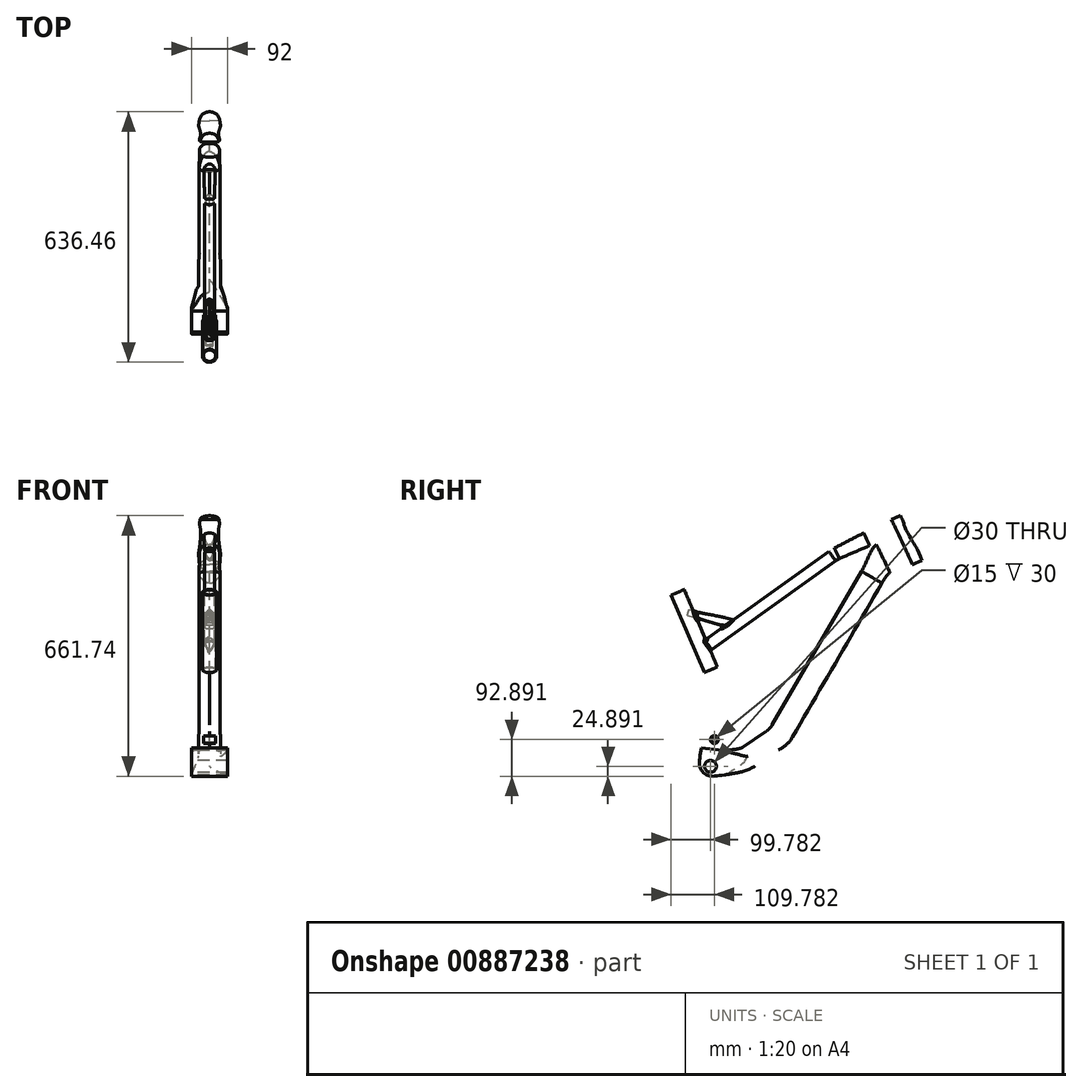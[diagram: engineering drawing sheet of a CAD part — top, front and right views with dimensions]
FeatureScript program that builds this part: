
annotation { "Feature Type Name" : "Feature", "Feature Type Description" : "" }
export const myFeature = defineFeature(function(context is Context, id is Id, definition is map)
    precondition{}
    {
        {
            var Q0;
            Q0=qCreatedBy(makeId("Right.planeOp"),FACE);
            var sketch = newSketch(context, id + "F0", { "sketchPlane" : qUnion([Q0])});
            skLineSegment(sketch, "E0", {"start": v(394.56, 392.73) * mm, "end": v(268.92, 334.44) * mm});
            skLineSegment(sketch, "E1", {"start": v(268.92, 334.44) * mm, "end": v(-58.18, 97.5) * mm});
            skLineSegment(sketch, "E2", {"start": v(359.7, 337.97) * mm, "end": v(273.68, 299.57) * mm});
            skLineSegment(sketch, "E3", {"start": v(273.68, 299.57) * mm, "end": v(-46.2, 69.7) * mm});
            skLineSegment(sketch, "E4", {"start": v(-106.05, 214.72) * mm, "end": v(-58.18, 103.33) * mm});
            skLineSegment(sketch, "E5", {"start": v(-138.56, 202.1) * mm, "end": v(-48.82, -12.93) * mm});
            skLineSegment(sketch, "E6", {"start": v(24.33, -178.16) * mm, "end": v(95.53, -133.4) * mm});
            skLineSegment(sketch, "E7", {"start": v(95.53, -133.4) * mm, "end": v(106.59, -124.69) * mm});
            skLineSegment(sketch, "E8", {"start": v(106.59, -124.69) * mm, "end": v(115.3, -114.9) * mm});
            skLineSegment(sketch, "E9", {"start": v(115.3, -114.9) * mm, "end": v(371.01, 330.47) * mm});
            skLineSegment(sketch, "E10", {"start": v(492.3, 300.77) * mm, "end": v(414.97, 263.1) * mm});
            skLineSegment(sketch, "E11", {"start": v(414.97, 263.1) * mm, "end": v(406.05, 257.63) * mm});
            skLineSegment(sketch, "E12", {"start": v(406.05, 257.63) * mm, "end": v(398.23, 251.01) * mm});
            skLineSegment(sketch, "E13", {"start": v(398.23, 251.01) * mm, "end": v(391.73, 242.37) * mm});
            skLineSegment(sketch, "E14", {"start": v(391.73, 242.37) * mm, "end": v(164.62, -148.47) * mm});
            skLineSegment(sketch, "E15", {"start": v(164.62, -148.47) * mm, "end": v(157.35, -161.15) * mm});
            skLineSegment(sketch, "E16", {"start": v(157.35, -161.15) * mm, "end": v(146.9, -170) * mm});
            skLineSegment(sketch, "E17", {"start": v(146.9, -170) * mm, "end": v(129.26, -182.49) * mm});
            skLineSegment(sketch, "E18", {"start": v(129.26, -182.49) * mm, "end": v(69.06, -222.74) * mm});
            skLineSegment(sketch, "E19", {"start": v(-65.83, -137.88) * mm, "end": v(-59.08, -90.58) * mm});
            skLineSegment(sketch, "E20", {"start": v(-59.08, -90.58) * mm, "end": v(-49.16, -39.89) * mm});
            skLineSegment(sketch, "E21", {"start": v(-49.16, -39.89) * mm, "end": v(-47.14, -26.82) * mm});
            skLineSegment(sketch, "E22", {"start": v(2.2, 4.26) * mm, "end": v(-21.46, -107.7) * mm});
            skLineSegment(sketch, "E23", {"start": v(-78.37, 170.94) * mm, "end": v(2.72, 153.82) * mm});
            skLineSegment(sketch, "E24", {"start": v(-78.8, 154.84) * mm, "end": v(-10.87, 135.06) * mm});
            skLineSegment(sketch, "E25", {"start": v(437.67, 414) * mm, "end": v(393.8, 394.32) * mm});
            skLineSegment(sketch, "E26", {"start": v(415.73, 404.16) * mm, "end": v(-44.38, 404.16) * mm});
            skLineSegment(sketch, "E27", {"start": v(-44.38, -222.84) * mm, "end": v(-44.38, 470.33) * mm});
            skLineSegment(sketch, "E28", {"start": v(-44.38, -222.84) * mm, "end": v(-220.5, 433.45) * mm});
            skLineSegment(sketch, "E29", {"start": v(-44.38, -222.84) * mm, "end": v(-34.38, -154.84) * mm});
            skCircle(sketch, "E30", {"center": v(-34.38, -154.84) * mm, "radius": 10 * mm});
            skCircle(sketch, "E31", {"center": v(-34.38, -154.84) * mm, "radius": 7.5 * mm});
            skLineSegment(sketch, "E32", {"start": v(415.73, 404.16) * mm, "end": v(497.16, 229.55) * mm});
            skPoint(sketch, "E33", {"position": v(422.14, 390.42) * mm});
            skPoint(sketch, "E34", {"position": v(432.88, 367.4) * mm});
            skPoint(sketch, "E35", {"position": v(454.56, 320.9) * mm});
            skPoint(sketch, "E36", {"position": v(469.2, 289.52) * mm});
            skFitSpline(sketch, "E37", {"points": [v(437.67, 414) * mm, v(443.95, 402.74) * mm, v(445.2, 399.5) * mm, v(452.3, 378.64) * mm, v(478.75, 333.33) * mm, v(480.29, 331) * mm, v(492.3, 300.77) * mm], "startDerivative": vector(88.16, -136) * mm, "endDerivative": vector(86.61, -241.27) * mm});
            skCircle(sketch, "E38", {"center": v(-44.38, -222.84) * mm, "radius": 15 * mm});
            skLineSegment(sketch, "E39", {"start": v(-13.68, -182.87) * mm, "end": v(-7.77, -244.28) * mm});
            skFitSpline(sketch, "E40", {"points": [v(-67.41, -175.9) * mm, v(-70.5, -226.93) * mm, v(-50.42, -245.86) * mm, v(-7.77, -244.28) * mm], "startDerivative": vector(-21.1, -148.4) * mm, "endDerivative": vector(183.55, 26.83) * mm});
            skLineSegment(sketch, "E41", {"start": v(-13.68, -182.87) * mm, "end": v(-67.41, -175.9) * mm});
            skFitSpline(sketch, "E42", {"points": [v(69.06, -222.74) * mm, v(33.55, -237.56) * mm, v(-7.77, -244.28) * mm], "startDerivative": vector(-87.67, -58.62) * mm, "endDerivative": vector(-97.3, -14.22) * mm});
            skSolve(sketch);
        }
        {
            var Q0;
            Q0=sQuery(id+"F0.wireOp",EDGE,"E14");
            var Q1;
            Q1=sQuery(id+"F0.wireOp",VERTEX,"E14.end");
            cPlane(context, id + "F1", {"entities" : qUnion([Q0, Q1]), "cplaneType" : CPlaneType.LINE_POINT, "offset" : 25 * mm, "width" : 150 * mm, "height" : 150 * mm});
        }
        {
            var Q0;
            Q0=qCreatedBy(id+"F1.planeOp",FACE);
            var sketch = newSketch(context, id + "F2", { "sketchPlane" : qUnion([Q0])});
            skFitSpline(sketch, "E43", {"points": [v(0, -216.2) * mm, v(11, -210.2) * mm, v(26, -168.2) * mm, v(20, -160.7) * mm, v(0, -156.2) * mm], "startDerivative": vector(27.72, -0.05) * mm, "endDerivative": vector(-102.66, 1.52) * mm});
            skLineSegment(sketch, "E44", {"start": v(0, 0) * mm, "end": v(0, -298.68) * mm});
            skFitSpline(sketch, "E45.MirrorCS", {"points": [v(0, -216.2) * mm, v(-11, -210.2) * mm, v(-26, -168.2) * mm, v(-20, -160.7) * mm, v(0, -156.2) * mm], "startDerivative": vector(-27.72, -0.05) * mm, "endDerivative": vector(102.66, 1.52) * mm});
            skSolve(sketch);
        }
        {
            var Q0;
            {var subQ0=sQuery(id+"F2.wireOp",EDGE,"E43");Q0=makeQuery(id+"F2.imprint","IMPRINT",FACE,{"disambiguationData":[TD([[makeQuery(id+"F2.imprint","IMPRINT",EDGE,{"derivedFrom":subQ0}),1.0]])]});}
            var Q1;
            {var subQ0=sQuery(id+"F2.wireOp",EDGE,"E45.MirrorCS");Q1=makeQuery(id+"F2.imprint","IMPRINT",FACE,{"disambiguationData":[TD([[makeQuery(id+"F2.imprint","IMPRINT",EDGE,{"derivedFrom":subQ0}),-1.0]])]});}
            var Q2;
            Q2=sQuery(id+"F0.wireOp",EDGE,"E14");
            sweep(context, id + "F3", {"profiles" : qUnion([Q0, Q1]), "path" : qUnion([Q2])});
        }
        {
            var Q0;
            Q0=sQuery(id+"F0.wireOp",VERTEX,"E18.end");
            var Q1;
            Q1=sQuery(id+"F0.wireOp",EDGE,"E18");
            cPlane(context, id + "F4", {"entities" : qUnion([Q0, Q1]), "cplaneType" : CPlaneType.LINE_POINT, "offset" : 25 * mm, "width" : 150 * mm, "height" : 150 * mm});
        }
        {
            var Q0;
            Q0=qCreatedBy(id+"F4.planeOp",FACE);
            var sketch = newSketch(context, id + "F5", { "sketchPlane" : qUnion([Q0])});
            skFitSpline(sketch, "E46", {"points": [v(0, -222.4) * mm, v(15.02, -221) * mm, v(24.08, -211.48) * mm, v(26.32, -171.97) * mm, v(21.9, -167.33) * mm, v(0, -165.4) * mm], "startDerivative": vector(103.75, 0.01) * mm, "endDerivative": vector(-157.98, 1.47) * mm});
            skFitSpline(sketch, "E47.MirrorCS", {"points": [v(0, -222.4) * mm, v(-15.02, -221) * mm, v(-24.08, -211.48) * mm, v(-26.32, -171.97) * mm, v(-21.9, -167.33) * mm, v(0, -165.4) * mm], "startDerivative": vector(-103.75, 0.01) * mm, "endDerivative": vector(157.98, 1.47) * mm});
            skSolve(sketch);
        }
        {
            var Q0;
            Q0=makeQuery(id+"F5.imprint","IMPRINT",FACE,{"disambiguationData":[TD([[makeQuery(id+"F5.imprint","IMPRINT",EDGE,{"derivedFrom":sQuery(id+"F5.wireOp",EDGE,"E46")}),1.0]])]});
            var Q1;
            Q1=sQuery(id+"F0.wireOp",EDGE,"E18");
            sweep(context, id + "F6", {"profiles" : qUnion([Q0]), "path" : qUnion([Q1])});
        }
        {
            var Q0;
            Q0=makeQuery(id+"F6.opSweep","CAP_FACE",FACE,{"disambiguationData":[OSD([sQuery(id+"F0.wireOp",VERTEX,"E18.start"),sQuery(id+"F5.wireOp",EDGE,"E46"),sQuery(id+"F5.wireOp",EDGE,"E47.MirrorCS")])],"isStart":false});
            var Q1;
            Q1=makeQuery(id+"F3.opSweep","CAP_FACE",FACE,{"disambiguationData":[OSD([sQuery(id+"F0.wireOp",VERTEX,"E14.end"),sQuery(id+"F2.wireOp",EDGE,"E43"),sQuery(id+"F2.wireOp",EDGE,"E45.MirrorCS")])],"isStart":true});
            loft(context, id + "F7", {"operationType" : NewBodyOperationType.ADD, "startCondition" : LoftEndDerivativeType.MATCH_CURVATURE, "startMagnitude" : 1, "endCondition" : LoftEndDerivativeType.MATCH_CURVATURE, "endMagnitude" : 1, "sheetProfilesArray" : [{ "sheetProfileEntities" : qUnion([Q0]) }, { "sheetProfileEntities" : qUnion([Q1]) }]});
        }
        {
            var Q0;
            Q0=sQuery(id+"F0.wireOp",VERTEX,"E10.end");
            var Q1;
            Q1=sQuery(id+"F0.wireOp",EDGE,"E10");
            cPlane(context, id + "F8", {"entities" : qUnion([Q0, Q1]), "cplaneType" : CPlaneType.LINE_POINT, "offset" : 25 * mm, "width" : 150 * mm, "height" : 150 * mm});
        }
        {
            var Q0;
            Q0=qCreatedBy(id+"F8.planeOp",FACE);
            var sketch = newSketch(context, id + "F9", { "sketchPlane" : qUnion([Q0])});
            skFitSpline(sketch, "E48", {"points": [v(0, 62.13) * mm, v(-9.68, 63.52) * mm, v(-19.4, 73.38) * mm, v(-25.78, 107.3) * mm, v(-23.62, 126.27) * mm, v(-16.86, 137.13) * mm, v(0, 141.08) * mm], "startDerivative": vector(-109.37, 0) * mm, "endDerivative": vector(154.62, 0) * mm});
            skFitSpline(sketch, "E49.MirrorCS", {"points": [v(0, 62.13) * mm, v(9.68, 63.52) * mm, v(19.4, 73.38) * mm, v(25.78, 107.3) * mm, v(23.62, 126.27) * mm, v(16.86, 137.13) * mm, v(0, 141.08) * mm], "startDerivative": vector(109.37, 0) * mm, "endDerivative": vector(-154.62, 0) * mm});
            skSolve(sketch);
        }
        {
            var Q0;
            Q0=makeQuery(id+"F3.opSweep","CAP_FACE",FACE,{"disambiguationData":[OSD([sQuery(id+"F0.wireOp",VERTEX,"E14.start"),sQuery(id+"F2.wireOp",EDGE,"E43"),sQuery(id+"F2.wireOp",EDGE,"E45.MirrorCS")])],"isStart":false});
            var Q1;
            Q1=makeQuery(id+"F9.imprint","IMPRINT",FACE,{"disambiguationData":[TD([[makeQuery(id+"F9.imprint","IMPRINT",EDGE,{"derivedFrom":sQuery(id+"F9.wireOp",EDGE,"E48")}),-1.0]])]});
            loft(context, id + "F10", {"operationType" : NewBodyOperationType.ADD, "startCondition" : LoftEndDerivativeType.NORMAL_TO_PROFILE, "startMagnitude" : 1, "endCondition" : LoftEndDerivativeType.NORMAL_TO_PROFILE, "endMagnitude" : 0.6, "sheetProfilesArray" : [{ "sheetProfileEntities" : qUnion([Q0]) }, { "sheetProfileEntities" : qUnion([Q1]) }]});
        }
        {
            var Q0;
            Q0=sQuery(id+"F0.wireOp",EDGE,"E3");
            var Q1;
            Q1=sQuery(id+"F0.wireOp",VERTEX,"E3.end");
            cPlane(context, id + "F11", {"entities" : qUnion([Q0, Q1]), "cplaneType" : CPlaneType.LINE_POINT, "offset" : 25 * mm, "width" : 150 * mm, "height" : 150 * mm});
        }
        {
            var Q0;
            Q0=qCreatedBy(id+"F11.planeOp",FACE);
            var sketch = newSketch(context, id + "F12", { "sketchPlane" : qUnion([Q0])});
            skFitSpline(sketch, "E50", {"points": [v(0, 83.57) * mm, v(1.95, 84.02) * mm, v(3.76, 85.96) * mm, v(12.1, 107.97) * mm, v(11.29, 109.77) * mm, v(0, 113.21) * mm], "startDerivative": vector(26.6, 0) * mm, "endDerivative": vector(-52.94, 0) * mm});
            skFitSpline(sketch, "E51.MirrorCS", {"points": [v(0, 83.57) * mm, v(-1.95, 84.02) * mm, v(-3.76, 85.96) * mm, v(-12.1, 107.97) * mm, v(-11.29, 109.77) * mm, v(0, 113.21) * mm], "startDerivative": vector(-26.6, 0) * mm, "endDerivative": vector(52.94, 0) * mm});
            skSolve(sketch);
        }
        {
            var Q0;
            Q0=makeQuery(id+"F12.imprint","IMPRINT",FACE,{"disambiguationData":[TD([[makeQuery(id+"F12.imprint","IMPRINT",EDGE,{"derivedFrom":sQuery(id+"F12.wireOp",EDGE,"E50")}),1.0]])]});
            var Q1;
            Q1=sQuery(id+"F0.wireOp",EDGE,"E3");
            sweep(context, id + "F13", {"profiles" : qUnion([Q0]), "path" : qUnion([Q1])});
        }
        {
            var Q0;
            Q0=sQuery(id+"F0.wireOp",VERTEX,"E0.end");
            var Q1;
            Q1=sQuery(id+"F0.wireOp",EDGE,"E0");
            cPlane(context, id + "F14", {"entities" : qUnion([Q0, Q1]), "cplaneType" : CPlaneType.LINE_POINT, "offset" : 25 * mm, "width" : 150 * mm, "height" : 150 * mm});
        }
        {
            var Q0;
            Q0=qCreatedBy(id+"F14.planeOp",FACE);
            var sketch = newSketch(context, id + "F15", { "sketchPlane" : qUnion([Q0])});
            skFitSpline(sketch, "E52", {"points": [v(0, 157.35) * mm, v(1.12, 157.46) * mm, v(3.44, 159.27) * mm, v(12.43, 181.5) * mm, v(12.27, 183.85) * mm, v(0, 187.53) * mm], "startDerivative": vector(14.46, -0.03) * mm, "endDerivative": vector(-71.7, 1.23) * mm});
            skFitSpline(sketch, "E53.MirrorCS", {"points": [v(0, 157.35) * mm, v(-1.12, 157.46) * mm, v(-3.44, 159.27) * mm, v(-12.43, 181.5) * mm, v(-12.27, 183.85) * mm, v(0, 187.53) * mm], "startDerivative": vector(-14.46, -0.03) * mm, "endDerivative": vector(71.7, 1.23) * mm});
            skSolve(sketch);
        }
        {
            var Q0;
            Q0=sQuery(id+"F0.wireOp",VERTEX,"E2.start");
            var Q1;
            Q1=sQuery(id+"F0.wireOp",EDGE,"E2");
            cPlane(context, id + "F16", {"entities" : qUnion([Q0, Q1]), "cplaneType" : CPlaneType.LINE_POINT, "offset" : 25 * mm, "width" : 150 * mm, "height" : 150 * mm});
        }
        {
            var Q0;
            Q0=qCreatedBy(id+"F16.planeOp",FACE);
            var sketch = newSketch(context, id + "F17", { "sketchPlane" : qUnion([Q0])});
            skFitSpline(sketch, "E54.MirrorCS", {"points": [v(0, 162) * mm, v(-3.1, 163) * mm, v(-7.1, 168.68) * mm, v(-14.14, 190.28) * mm, v(-13.47, 193.65) * mm, v(0, 197.04) * mm], "startDerivative": vector(-26.6, 0.06) * mm, "endDerivative": vector(71.7, 1.23) * mm});
            skFitSpline(sketch, "E55.MirrorCS", {"points": [v(0, 162) * mm, v(3.1, 163) * mm, v(7.1, 168.68) * mm, v(14.14, 190.28) * mm, v(13.47, 193.65) * mm, v(0, 197.04) * mm], "startDerivative": vector(26.6, 0.06) * mm, "endDerivative": vector(-71.7, 1.23) * mm});
            skSolve(sketch);
        }
        {
            var Q0;
            Q0=makeQuery(id+"F17.imprint","IMPRINT",FACE,{"disambiguationData":[TD([[makeQuery(id+"F17.imprint","IMPRINT",EDGE,{"derivedFrom":sQuery(id+"F17.wireOp",EDGE,"E54.MirrorCS")}),-1.0]])]});
            var Q1;
            Q1=makeQuery(id+"F15.imprint","IMPRINT",FACE,{"disambiguationData":[TD([[makeQuery(id+"F15.imprint","IMPRINT",EDGE,{"derivedFrom":sQuery(id+"F15.wireOp",EDGE,"E52")}),1.0]])]});
            loft(context, id + "F18", {"startCondition" : LoftEndDerivativeType.NORMAL_TO_PROFILE, "startMagnitude" : 1, "endCondition" : LoftEndDerivativeType.NORMAL_TO_PROFILE, "endMagnitude" : 1, "sheetProfilesArray" : [{ "sheetProfileEntities" : qUnion([Q0]) }, { "sheetProfileEntities" : qUnion([Q1]) }]});
        }
        {
            var Q1;
            Q1=makeQuery(id+"F13.opSweep","CAP_FACE",FACE,{"disambiguationData":[OSD([sQuery(id+"F0.wireOp",VERTEX,"E3.start"),sQuery(id+"F12.wireOp",EDGE,"E50"),sQuery(id+"F12.wireOp",EDGE,"E51.MirrorCS")])],"isStart":false});
            var Q2;
            Q2=makeQuery(id+"F18.opLoft","CAP_FACE",FACE,{"disambiguationData":[OSD([makeQuery(id+"F15.imprint","IMPRINT",FACE,{"disambiguationData":[TD([[makeQuery(id+"F15.imprint","IMPRINT",EDGE,{"derivedFrom":sQuery(id+"F15.wireOp",EDGE,"E52")}),1.0]])]})])],"isStart":true});
            loft(context, id + "F19", {"operationType" : NewBodyOperationType.ADD, "startCondition" : LoftEndDerivativeType.NORMAL_TO_PROFILE, "startMagnitude" : 0.5, "endCondition" : LoftEndDerivativeType.NORMAL_TO_PROFILE, "endMagnitude" : 0.5, "sheetProfilesArray" : [{ "sheetProfileEntities" : qUnion([Q1]) }, { "sheetProfileEntities" : qUnion([Q2]) }]});
        }
        {
            var Q0;
            Q0=sQuery(id+"F0.wireOp",VERTEX,"E4.end");
            var Q1;
            Q1=sQuery(id+"F0.wireOp",EDGE,"E4");
            cPlane(context, id + "F20", {"entities" : qUnion([Q0, Q1]), "cplaneType" : CPlaneType.LINE_POINT, "offset" : 25 * mm, "width" : 150 * mm, "height" : 150 * mm});
        }
        {
            var Q0;
            Q0=qCreatedBy(id+"F20.planeOp",FACE);
            var sketch = newSketch(context, id + "F21", { "sketchPlane" : qUnion([Q0])});
            skCircle(sketch, "E56", {"center": v(0, 30.64) * mm, "radius": 15.8 * mm});
            skCircle(sketch, "E57", {"center": v(0, 30.64) * mm, "radius": 18 * mm});
            skSolve(sketch);
        }
        {
            var Q0;
            Q0=makeQuery(id+"F21.imprint","IMPRINT",FACE,{"disambiguationData":[TD([[makeQuery(id+"F21.imprint","IMPRINT",EDGE,{"derivedFrom":sQuery(id+"F21.wireOp",EDGE,"E56")}),-1.0]])]});
            extrude(context, id + "F22", {"entities" : qUnion([Q0]), "operationType" : NewBodyOperationType.ADD, "depth" : 80 * mm, "offsetDistance" : 25 * mm});
        }
        {
            var Q0;
            Q0=makeQuery(id+"F22.opExtrude","CAP_FACE",FACE,{"disambiguationData":[OSD([sQuery(id+"F21.wireOp",EDGE,"E56"),sQuery(id+"F21.wireOp",EDGE,"E57")])],"isStart":true});
            extrude(context, id + "F23", {"entities" : qUnion([Q0]), "operationType" : NewBodyOperationType.ADD, "depth" : 134 * mm, "offsetDistance" : 25 * mm});
        }
        {
            var Q0;
            Q0=sQuery(id+"F0.wireOp",VERTEX,"E24.start");
            var Q1;
            Q1=sQuery(id+"F0.wireOp",EDGE,"E24");
            cPlane(context, id + "F24", {"entities" : qUnion([Q0, Q1]), "cplaneType" : CPlaneType.LINE_POINT, "offset" : 25 * mm, "width" : 150 * mm, "height" : 150 * mm});
        }
        {
            var Q0;
            Q0=sQuery(id+"F0.wireOp",VERTEX,"E24.end");
            var Q1;
            Q1=sQuery(id+"F0.wireOp",EDGE,"E24");
            cPlane(context, id + "F25", {"entities" : qUnion([Q0, Q1]), "cplaneType" : CPlaneType.LINE_POINT, "offset" : 25 * mm, "width" : 150 * mm, "height" : 150 * mm});
        }
        {
            var Q0;
            Q0=qCreatedBy(id+"F24.planeOp",FACE);
            var sketch = newSketch(context, id + "F26", { "sketchPlane" : qUnion([Q0])});
            skFitSpline(sketch, "E58", {"points": [v(0, 125.66) * mm, v(-7.65, 126.67) * mm, v(-8.56, 128) * mm, v(-6.36, 135.83) * mm, v(-1.91, 140.47) * mm, v(-0.96, 140.93) * mm, v(0, 141.05) * mm], "startDerivative": vector(-44.41, 0) * mm, "endDerivative": vector(17.18, 0) * mm});
            skFitSpline(sketch, "E59.MirrorCS", {"points": [v(0, 125.66) * mm, v(7.65, 126.67) * mm, v(8.56, 128) * mm, v(6.36, 135.83) * mm, v(1.91, 140.47) * mm, v(0.96, 140.93) * mm, v(0, 141.05) * mm], "startDerivative": vector(44.41, 0) * mm, "endDerivative": vector(-17.18, 0) * mm});
            skSolve(sketch);
        }
        {
            var Q0;
            Q0=qCreatedBy(id+"F25.planeOp",FACE);
            var sketch = newSketch(context, id + "F27", { "sketchPlane" : qUnion([Q0])});
            skFitSpline(sketch, "E60", {"points": [v(0, 125.4) * mm, v(-7.88, 126.3) * mm, v(-9.51, 128.26) * mm, v(-7.77, 138.38) * mm, v(-2.55, 145.94) * mm, v(0, 146.94) * mm], "startDerivative": vector(-44.41, 0) * mm, "endDerivative": vector(23.48, 0.75) * mm});
            skFitSpline(sketch, "E61.MirrorCS", {"points": [v(0, 125.4) * mm, v(7.88, 126.3) * mm, v(9.51, 128.26) * mm, v(7.77, 138.38) * mm, v(2.55, 145.94) * mm, v(0, 146.94) * mm], "startDerivative": vector(44.41, 0) * mm, "endDerivative": vector(-23.48, 0.75) * mm});
            skSolve(sketch);
        }
        {
            var Q0;
            Q0=makeQuery(id+"F26.imprint","IMPRINT",FACE,{"disambiguationData":[TD([[makeQuery(id+"F26.imprint","IMPRINT",EDGE,{"derivedFrom":sQuery(id+"F26.wireOp",EDGE,"E58")}),-1.0]])]});
            var Q1;
            Q1=makeQuery(id+"F27.imprint","IMPRINT",FACE,{"disambiguationData":[TD([[makeQuery(id+"F27.imprint","IMPRINT",EDGE,{"derivedFrom":sQuery(id+"F27.wireOp",EDGE,"E60")}),-1.0]])]});
            loft(context, id + "F28", {"startCondition" : LoftEndDerivativeType.NORMAL_TO_PROFILE, "startMagnitude" : 0.5, "endCondition" : LoftEndDerivativeType.NORMAL_TO_PROFILE, "endMagnitude" : 0.5, "sheetProfilesArray" : [{ "sheetProfileEntities" : qUnion([Q0]) }, { "sheetProfileEntities" : qUnion([Q1]) }]});
        }
        {
            var Q0;
            Q0=makeQuery(id+"F28.opLoft","CAP_FACE",FACE,{"disambiguationData":[OSD([makeQuery(id+"F27.imprint","IMPRINT",FACE,{"disambiguationData":[TD([[makeQuery(id+"F27.imprint","IMPRINT",EDGE,{"derivedFrom":sQuery(id+"F27.wireOp",EDGE,"E60")}),-1.0]])]})])],"isStart":true});
            extrude(context, id + "F29", {"entities" : qUnion([Q0]), "operationType" : NewBodyOperationType.ADD, "depth" : 20 * mm, "offsetDistance" : 25 * mm});
        }
        {
            var Q0;
            Q0=makeQuery(id+"F28.opLoft","CAP_FACE",FACE,{"disambiguationData":[OSD([makeQuery(id+"F26.imprint","IMPRINT",FACE,{"disambiguationData":[TD([[makeQuery(id+"F26.imprint","IMPRINT",EDGE,{"derivedFrom":sQuery(id+"F26.wireOp",EDGE,"E58")}),-1.0]])]})])],"isStart":true});
            extrude(context, id + "F30", {"entities" : qUnion([Q0]), "operationType" : NewBodyOperationType.ADD, "depth" : 25 * mm, "offsetDistance" : 25 * mm});
        }
        {
            var Q0;
            {var subQ0=sQuery(id+"F27.wireOp",EDGE,"E61.MirrorCS");var subQ1=sQuery(id+"F27.wireOp",EDGE,"E60");var subQ2=sQuery(id+"F12.wireOp",EDGE,"E50");var subQ3=sQuery(id+"F0.wireOp",EDGE,"E3");var subQ4=sQuery(id+"F15.wireOp",EDGE,"E52");var subQ5=sQuery(id+"F15.wireOp",EDGE,"E53.MirrorCS");var subQ6=makeQuery(id+"F15.imprint","INTERSECT",VERTEX,{"disambiguationData":[OD(1.0)],"derivedFrom":[subQ4,subQ5]});var subQ7=makeQuery(id+"F15.imprint","INTERSECT",VERTEX,{"disambiguationData":[OD(0.0)],"derivedFrom":[subQ4,subQ5]});var subQ8=makeQuery(id+"F18.opLoft","MID_CAP_VERTEX",VERTEX,{"disambiguationData":[OSD([subQ4,subQ5]),TDD([subQ6])],"capPos":1.0});var subQ9=makeQuery(id+"F18.opLoft","MID_CAP_VERTEX",VERTEX,{"disambiguationData":[OSD([subQ4,subQ5]),TDD([subQ7])],"capPos":1.0});var subQ10=sQuery(id+"F0.wireOp",VERTEX,"E3.start");var subQ11=sQuery(id+"F12.wireOp",EDGE,"E51.MirrorCS");var subQ12=makeQuery(id+"F13.opSweep","CAP_VERTEX",VERTEX,{"disambiguationData":[OSD([subQ3,subQ2,subQ11]),TDD([subQ3,makeQuery(id+"F12.imprint","INTERSECT",VERTEX,{"disambiguationData":[OD(1.0)],"derivedFrom":[subQ2,subQ11]})])],"isStart":false});var subQ13=makeQuery(id+"F13.opSweep","CAP_VERTEX",VERTEX,{"disambiguationData":[OSD([subQ3,subQ2,subQ11]),TDD([subQ3,makeQuery(id+"F12.imprint","INTERSECT",VERTEX,{"disambiguationData":[OD(0.0)],"derivedFrom":[subQ2,subQ11]})])],"isStart":false});Q0=makeQuery(id+"F29.boolean.opBoolean","INTERSECT",EDGE,{"derivedFrom":[makeQuery(id+"F22.boolean.opBoolean","SPLIT",FACE,{"disambiguationData":[TD([makeQuery(id+"F13.opSweep","SWEPT_FACE",FACE,{"disambiguationData":[OSD([subQ3,subQ2])]}),makeQuery(id+"F19.opLoft","SWEPT_FACE",FACE,{"disambiguationData":[OSD([subQ10,subQ3,subQ2,subQ11,subQ4,subQ5]),TDD([subQ13,subQ12,makeQuery(id+"F13.opSweep","CAP_EDGE",EDGE,{"disambiguationData":[OSD([subQ10,subQ2])],"isStart":false}),subQ9,subQ8,makeQuery(id+"F18.opLoft","MID_CAP_EDGE",EDGE,{"disambiguationData":[OSD([subQ4,subQ5]),TDD([subQ7,subQ6,makeQuery(id+"F15.imprint","IMPRINT",EDGE,{"derivedFrom":subQ4})])],"capPos":1.0})])]}),makeQuery(id+"F19.opLoft","SWEPT_FACE",FACE,{"disambiguationData":[OSD([subQ10,subQ3,subQ2,subQ11,subQ4,subQ5]),TDD([subQ13,subQ12,makeQuery(id+"F13.opSweep","CAP_EDGE",EDGE,{"disambiguationData":[OSD([subQ10,subQ11])],"isStart":false}),subQ9,subQ8,makeQuery(id+"F18.opLoft","MID_CAP_EDGE",EDGE,{"disambiguationData":[OSD([subQ4,subQ5]),TDD([subQ7,subQ6,makeQuery(id+"F15.imprint","IMPRINT",EDGE,{"derivedFrom":subQ5})])],"capPos":1.0})])]}),makeQuery(id+"F22.opExtrude","SWEPT_FACE",FACE,{"disambiguationData":[OSD([sQuery(id+"F21.wireOp",EDGE,"E57")])]})])],"derivedFrom":makeQuery(id+"F13.opSweep","SWEPT_FACE",FACE,{"disambiguationData":[OSD([subQ3,subQ11])]})}),makeQuery(id+"F29.opExtrude","SWEPT_FACE",FACE,{"disambiguationData":[OSD([subQ1,subQ0]),TDD([makeQuery(id+"F28.opLoft","MID_CAP_EDGE",EDGE,{"disambiguationData":[OSD([subQ1,subQ0]),TDD([makeQuery(id+"F27.imprint","INTERSECT",VERTEX,{"disambiguationData":[OD(0.0)],"derivedFrom":[subQ1,subQ0]}),makeQuery(id+"F27.imprint","INTERSECT",VERTEX,{"disambiguationData":[OD(1.0)],"derivedFrom":[subQ1,subQ0]}),makeQuery(id+"F27.imprint","IMPRINT",EDGE,{"derivedFrom":subQ0})])],"capPos":1.0})])]})]});}
            var Q1;
            Q1=makeQuery(id+"F22.boolean.opBoolean","INTERSECT",EDGE,{"derivedFrom":[makeQuery(id+"F13.opSweep","SWEPT_FACE",FACE,{"disambiguationData":[OSD([sQuery(id+"F0.wireOp",EDGE,"E3"),sQuery(id+"F12.wireOp",EDGE,"E51.MirrorCS")])]}),makeQuery(id+"F22.opExtrude","SWEPT_FACE",FACE,{"disambiguationData":[OSD([sQuery(id+"F21.wireOp",EDGE,"E57")])]})]});
            var Q2;
            {var subQ0=sQuery(id+"F26.wireOp",EDGE,"E58");var subQ1=sQuery(id+"F26.wireOp",EDGE,"E59.MirrorCS");var subQ2=sQuery(id+"F21.wireOp",EDGE,"E57");Q2=makeQuery(id+"F30.boolean.opBoolean","INTERSECT",EDGE,{"derivedFrom":[makeQuery(id+"F23.boolean.opBoolean","MERGE",FACE,{"derivedFrom":[makeQuery(id+"F22.opExtrude","SWEPT_FACE",FACE,{"disambiguationData":[OSD([subQ2])]}),makeQuery(id+"F23.opExtrude","SWEPT_FACE",FACE,{"disambiguationData":[OSD([subQ2])]})]}),makeQuery(id+"F30.opExtrude","SWEPT_FACE",FACE,{"disambiguationData":[OSD([subQ0,subQ1]),TDD([makeQuery(id+"F28.opLoft","MID_CAP_EDGE",EDGE,{"disambiguationData":[OSD([subQ0,subQ1]),TDD([makeQuery(id+"F26.imprint","INTERSECT",VERTEX,{"disambiguationData":[OD(0.0)],"derivedFrom":[subQ0,subQ1]}),makeQuery(id+"F26.imprint","INTERSECT",VERTEX,{"disambiguationData":[OD(1.0)],"derivedFrom":[subQ0,subQ1]}),makeQuery(id+"F26.imprint","IMPRINT",EDGE,{"derivedFrom":subQ0})])],"capPos":0.0})])]})]});}
            fillet(context, id + "F31", {"entities" : qUnion([Q0, Q1, Q2]), "radius" : 6 * mm, "tangentPropagation" : true, "allowEdgeOverflow" : false});
        }
        {
            var Q0;
            Q0=makeQuery(id+"F0.imprint","IMPRINT",FACE,{"disambiguationData":[TD([[makeQuery(id+"F0.imprint","IMPRINT",EDGE,{"derivedFrom":sQuery(id+"F0.wireOp",EDGE,"E31")}),-1.0]])]});
            extrude(context, id + "F32", {"entities" : qUnion([Q0]), "depth" : 30 * mm, "offsetDistance" : 25 * mm, "symmetric" : true});
        }
        {
            var Q0;
            {var subQ0=sQuery(id+"F0.wireOp",EDGE,"E37");Q0=makeQuery(id+"F0.imprint","IMPRINT",FACE,{"disambiguationData":[TD([[makeQuery(id+"F0.imprint","IMPRINT",EDGE,{"derivedFrom":subQ0}),-1.0]])]});}
            var Q1;
            Q1=sQuery(id+"F0.wireOp",EDGE,"E32");
            revolve(context, id + "F33", {"surfaceOperationType" : NewSurfaceOperationType.NEW, "entities" : qUnion([Q0]), "axis" : qUnion([Q1]), "revolveType" : RevolveType.SYMMETRIC, "angle" : 180 * degree});
        }
        {
            var Q0;
            {var subQ7=sQuery(id+"F0.wireOp",EDGE,"E39");Q0=makeQuery(id+"F0.imprint","IMPRINT",FACE,{"disambiguationData":[TD([[makeQuery(id+"F0.imprint","IMPRINT",EDGE,{"derivedFrom":subQ7}),-1.0]])]});}
            var Q1;
            {var subQ0=sQuery(id+"F0.wireOp",EDGE,"E41");var subQ1=sQuery(id+"F0.wireOp",EDGE,"E27");var subQ2=makeQuery(id+"F0.imprint","INTERSECT",VERTEX,{"derivedFrom":[subQ1,subQ0]});Q1=makeQuery(id+"F0.imprint","IMPRINT",FACE,{"disambiguationData":[TD([[makeQuery(id+"F0.imprint","IMPRINT",EDGE,{"disambiguationData":[TD([[subQ2,1.0]])],"derivedFrom":subQ1}),-1.0]])]});}
            var Q2;
            {var subQ0=sQuery(id+"F0.wireOp",EDGE,"E41");var subQ1=sQuery(id+"F0.wireOp",EDGE,"E27");var subQ2=makeQuery(id+"F0.imprint","INTERSECT",VERTEX,{"derivedFrom":[subQ1,subQ0]});Q2=makeQuery(id+"F0.imprint","IMPRINT",FACE,{"disambiguationData":[TD([[makeQuery(id+"F0.imprint","IMPRINT",EDGE,{"disambiguationData":[TD([[subQ2,1.0]])],"derivedFrom":subQ1}),1.0]])]});}
            extrude(context, id + "F34", {"entities" : qUnion([Q0, Q1, Q2]), "depth" : 92 * mm, "offsetDistance" : 25 * mm, "symmetric" : true});
        }
        {
            var Q0;
            Q0=sQuery(id+"F0.wireOp",EDGE,"E42");
            var Q2;
            Q2=makeQuery(id+"F34.opExtrude","SWEPT_FACE",FACE,{"disambiguationData":[OSD([sQuery(id+"F0.wireOp",EDGE,"E39")])]});
            var Q3;
            Q3=makeQuery(id+"F6.opSweep","CAP_FACE",FACE,{"disambiguationData":[OSD([sQuery(id+"F0.wireOp",VERTEX,"E18.end"),sQuery(id+"F5.wireOp",EDGE,"E46"),sQuery(id+"F5.wireOp",EDGE,"E47.MirrorCS")])],"isStart":true});
            var Q4;
            {var subQ0=sQuery(id+"F5.wireOp",EDGE,"E47.MirrorCS");var subQ1=sQuery(id+"F5.wireOp",EDGE,"E46");var subQ2=sQuery(id+"F0.wireOp",EDGE,"E18");Q4=makeQuery(id+"F6.opSweep","CAP_VERTEX",VERTEX,{"disambiguationData":[OSD([subQ2,subQ1,subQ0]),TDD([subQ2,makeQuery(id+"F5.imprint","INTERSECT",VERTEX,{"disambiguationData":[OD(1.0)],"derivedFrom":[subQ1,subQ0]})])],"isStart":true});}
            var Q5;
            Q5=sQuery(id+"F0.wireOp",VERTEX,"E39.start");
            loft(context, id + "F35", {"operationType" : NewBodyOperationType.ADD, "addSections" : true, "spine" : qUnion([Q0]), "sectionCount" : 5, "startCondition" : LoftEndDerivativeType.NORMAL_TO_PROFILE, "startMagnitude" : 1, "endCondition" : LoftEndDerivativeType.NORMAL_TO_PROFILE, "endMagnitude" : 1, "sheetProfilesArray" : [{ "sheetProfileEntities" : qUnion([Q2]) }, { "sheetProfileEntities" : qUnion([Q3]) }], "connections" : [{ "connectionEntities" : qUnion([Q4, Q5]), "connectionEdgeQueries" : qUnion([]), "connectionEdgeParameters" : [] }]});
        }
    });
